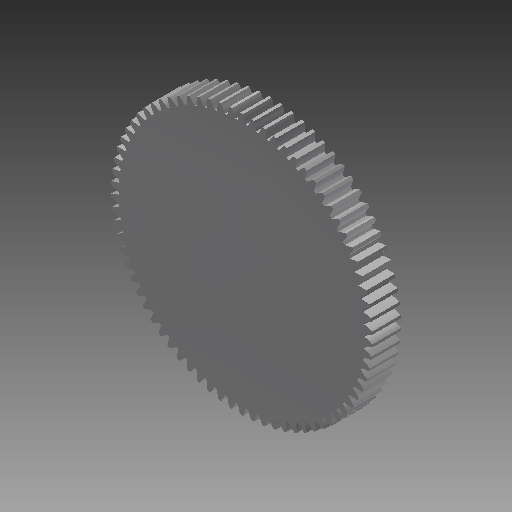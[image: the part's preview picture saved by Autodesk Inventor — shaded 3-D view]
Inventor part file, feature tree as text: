
AUTODESK INVENTOR PART (.ipt)
format: ipt  version: 2019 (Build 230136000, 136)  size: 439,808 bytes
history: native  units: mm (DEFAULTED — no unit token found)
features: plane x3, other x3, sketch x2, extrude x1
ambient origin geometry x8: Origin, YZ Plane, XZ Plane, XY Plane, X Axis, Y Axis, Z Axis, Center Point
bodies: Solid1 (feature_tree)
feature tree (9):
  extrude  "Extrusion1"  Depth=25.0mm TaperAngle=0.0deg
  plane  "Work Plane2"
  plane  "Work Plane8"
  plane  "Work Plane9"
  other  "Spur Gear"
  sketch  "Sketch1"  dims[d0=228.492427mm d1=25.0mm d2=0.0mm]
  sketch  "Sketch2"  dims[d3=222.496644mm d4=10.0mm d5=0.0mm d16=224.0mm d17=0.0mm d34=0.42454mm d39=0.0mm d41=0.0mm d43=224.0mm d46=224.0mm d47=0.0mm d48=0.0mm]
  other  "Srf1"
  other  "Pitch Diameter"
